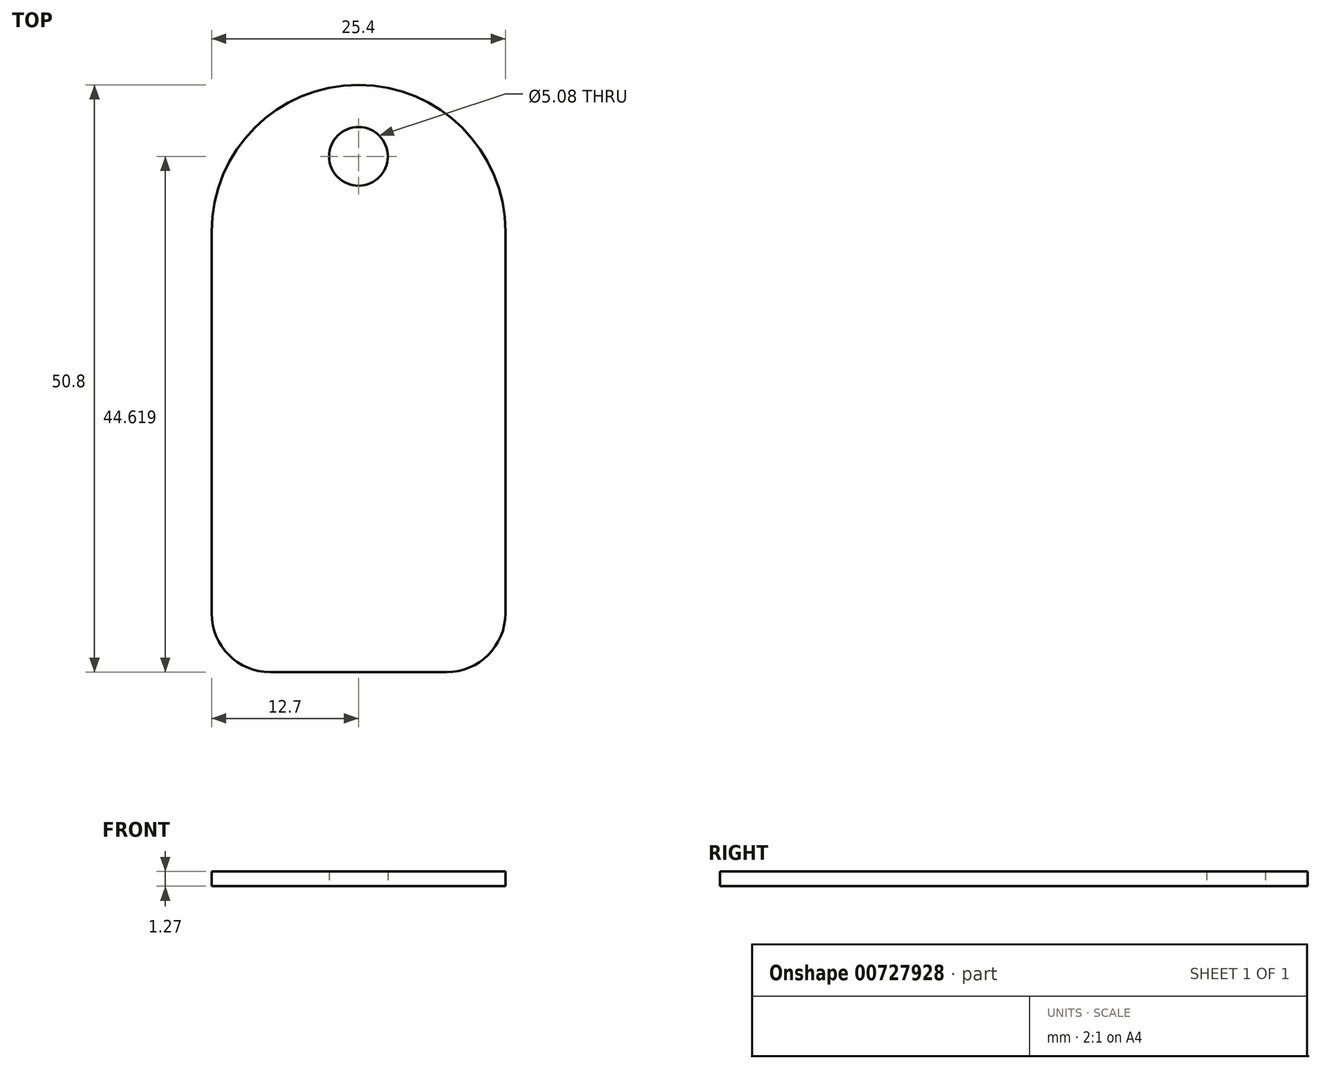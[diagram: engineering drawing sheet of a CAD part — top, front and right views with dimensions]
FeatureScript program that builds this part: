
annotation { "Feature Type Name" : "Feature", "Feature Type Description" : "" }
export const myFeature = defineFeature(function(context is Context, id is Id, definition is map)
    precondition{}
    {
        {
            var Q0;
            Q0=qCreatedBy(makeId("Top.planeOp"),FACE);
            var sketch = newSketch(context, id + "F0", { "sketchPlane" : qUnion([Q0])});
            skLineSegment(sketch, "E0.bottom", {"start": v(12.7, -19.05) * mm, "end": v(-12.7, -19.05) * mm});
            skLineSegment(sketch, "E0.left", {"start": v(12.7, -19.05) * mm, "end": v(12.7, 19.05) * mm});
            skLineSegment(sketch, "E0.right", {"start": v(-12.7, -19.05) * mm, "end": v(-12.7, 19.05) * mm});
            skPoint(sketch, "E0.middle", {"position": v(0, 0) * mm});
            skArc(sketch, "E1", {"start": v(12.7, 19.05) * mm, "mid": v(0, 31.75) * mm, "end": v(-12.7, 19.05) * mm});
            skCircle(sketch, "E2", {"center": v(0, 25.57) * mm, "radius": 2.54 * mm});
            skSolve(sketch);
        }
        {
            var Q0;
            Q0=makeQuery(id+"F0.imprint","IMPRINT",FACE,{"disambiguationData":[TD([[makeQuery(id+"F0.imprint","IMPRINT",EDGE,{"derivedFrom":sQuery(id+"F0.wireOp",EDGE,"E0.bottom")}),-1.0]])]});
            extrude(context, id + "F1", {"entities" : qUnion([Q0]), "depth" : 1.27 * mm, "offsetDistance" : 25.4 * mm});
        }
        {
            var Q0;
            Q0=makeQuery(id+"F1.opExtrude","SWEPT_EDGE",EDGE,{"disambiguationData":[OSD([sQuery(id+"F0.wireOp",EDGE,"E0.bottom"),sQuery(id+"F0.wireOp",EDGE,"E0.right")])]});
            var Q1;
            Q1=makeQuery(id+"F1.opExtrude","SWEPT_EDGE",EDGE,{"disambiguationData":[OSD([sQuery(id+"F0.wireOp",EDGE,"E0.bottom"),sQuery(id+"F0.wireOp",EDGE,"E0.left")])]});
            fillet(context, id + "F2", {"entities" : qUnion([Q0, Q1]), "radius" : 5.08 * mm, "tangentPropagation" : true, "allowEdgeOverflow" : false});
        }
    });
